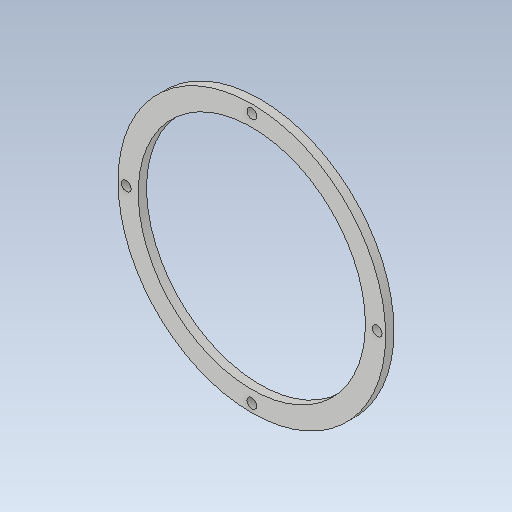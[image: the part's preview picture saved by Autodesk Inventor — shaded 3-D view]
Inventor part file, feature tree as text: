
AUTODESK INVENTOR PART (.ipt)
format: ipt  version: 2020.1 (Build 241239000, 239)  size: 107,520 bytes
history: native  units: mm
features: extrude x1, sketch x1
ambient origin geometry x8: Origin, YZ Plane, XZ Plane, XY Plane, X Axis, Y Axis, Z Axis, Center Point
bodies: Solid1 (feature_tree)
feature tree (2):
  extrude  "Extrusion1"  Depth=3.0mm
  sketch  "Sketch1"  dims[d0=96.0mm d1=81.5mm d2=45.0mm d3=3.5mm d4=40.0mm d6=360.0deg d8=3.0mm d9=0.0mm]
